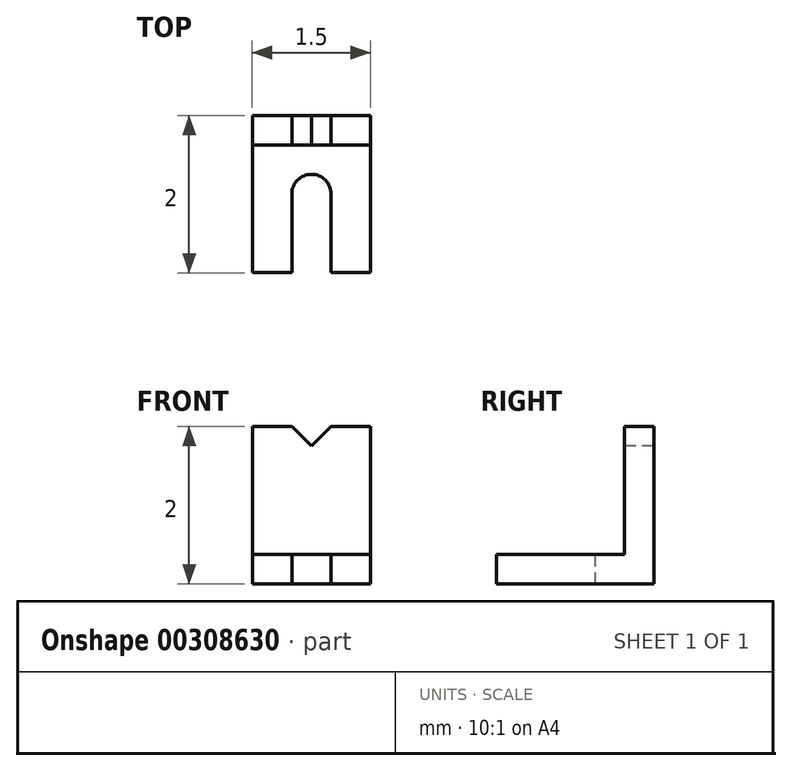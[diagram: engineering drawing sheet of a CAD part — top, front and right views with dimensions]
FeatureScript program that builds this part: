
annotation { "Feature Type Name" : "Feature", "Feature Type Description" : "" }
export const myFeature = defineFeature(function(context is Context, id is Id, definition is map)
    precondition{}
    {
        {
            var Q0;
            Q0=qCreatedBy(makeId("Top.planeOp"),FACE);
            var sketch = newSketch(context, id + "F0", { "sketchPlane" : qUnion([Q0])});
            skLineSegment(sketch, "E0.bottom", {"start": v(-24.74, -5.45) * mm, "end": v(-23.24, -5.45) * mm});
            skLineSegment(sketch, "E0.top", {"start": v(-24.74, -7.45) * mm, "end": v(-24.24, -7.45) * mm});
            skLineSegment(sketch, "E0.left", {"start": v(-24.74, -5.45) * mm, "end": v(-24.74, -7.45) * mm});
            skLineSegment(sketch, "E0.right", {"start": v(-23.24, -5.45) * mm, "end": v(-23.24, -7.45) * mm});
            skPoint(sketch, "E1", {"position": v(-23.74, -7.45) * mm});
            skPoint(sketch, "E2", {"position": v(-24.24, -7.45) * mm});
            skLineSegment(sketch, "E3", {"start": v(-23.74, -7.45) * mm, "end": v(-23.74, -6.45) * mm});
            skLineSegment(sketch, "E4", {"start": v(-24.24, -7.45) * mm, "end": v(-24.24, -6.45) * mm});
            skPoint(sketch, "E5.start.orphan", {"position": v(-23.99, -7.45) * mm});
            skLineSegment(sketch, "E6.trimOffspring", {"start": v(-23.74, -7.45) * mm, "end": v(-23.24, -7.45) * mm});
            skArc(sketch, "E7", {"start": v(-23.74, -6.45) * mm, "mid": v(-23.99, -6.2) * mm, "end": v(-24.24, -6.45) * mm});
            skSolve(sketch);
        }
        {
            var Q0;
            Q0 = qSketchRegion(id + "F0", true);
            extrude(context, id + "F1", {"entities" : qUnion([Q0]), "depth" : .375 * mm});
        }
        {
            var Q0;
            Q0=makeQuery(id+"F1.opExtrude","CAP_FACE",FACE,{"disambiguationData":[OSD([sQuery(id+"F0.wireOp",EDGE,"E0.bottom"),sQuery(id+"F0.wireOp",EDGE,"E0.top"),sQuery(id+"F0.wireOp",EDGE,"E0.left"),sQuery(id+"F0.wireOp",EDGE,"E0.right"),sQuery(id+"F0.wireOp",EDGE,"E3"),sQuery(id+"F0.wireOp",EDGE,"E4"),sQuery(id+"F0.wireOp",EDGE,"IjzjskDy-WpeZ-cA95-hpny-uStXZe4uYbSk"),sQuery(id+"F0.wireOp",EDGE,"E6.trimOffspring")])],"isStart":false});
            var sketch = newSketch(context, id + "F2", { "sketchPlane" : qUnion([Q0])});
            skLineSegment(sketch, "E8.bottom", {"start": v(-24.74, -5.45) * mm, "end": v(-23.24, -5.45) * mm});
            skLineSegment(sketch, "E8.top", {"start": v(-24.74, -5.82) * mm, "end": v(-23.24, -5.82) * mm});
            skLineSegment(sketch, "E8.left", {"start": v(-24.74, -5.45) * mm, "end": v(-24.74, -5.82) * mm});
            skLineSegment(sketch, "E8.right", {"start": v(-23.24, -5.45) * mm, "end": v(-23.24, -5.82) * mm});
            skSolve(sketch);
        }
        {
            var Q0;
            Q0 = qSketchRegion(id + "F2", true);
            extrude(context, id + "F3", {"entities" : qUnion([Q0]), "operationType" : NewBodyOperationType.ADD, "depth" : 1.62 * mm});
        }
        {
            var Q0;
            Q0=makeQuery(id+"F3.opExtrude","SWEPT_FACE",FACE,{"disambiguationData":[OSD([sQuery(id+"F2.wireOp",EDGE,"E8.top")])]});
            var sketch = newSketch(context, id + "F4", { "sketchPlane" : qUnion([Q0])});
            skPoint(sketch, "E9", {"position": v(-24.24, 2) * mm});
            skPoint(sketch, "E10", {"position": v(-23.74, 2) * mm});
            skPoint(sketch, "E11", {"position": v(-23.99, 1.75) * mm});
            skLineSegment(sketch, "E12", {"start": v(-24.24, 2) * mm, "end": v(-23.99, 1.75) * mm});
            skLineSegment(sketch, "E13", {"start": v(-23.74, 2) * mm, "end": v(-23.99, 1.75) * mm});
            skSolve(sketch);
        }
        {
            var Q0;
            {var subQ0=sQuery(id+"F4.wireOp",EDGE,"E12");Q0=makeQuery(id+"F4.imprint","IMPRINT",FACE,{"disambiguationData":[TD([[makeQuery(id+"F4.imprint","IMPRINT",EDGE,{"derivedFrom":subQ0}),1.0]])]});}
            extrude(context, id + "F5", {"entities" : qUnion([Q0]), "operationType" : NewBodyOperationType.REMOVE, "endBound" : BoundingType.UP_TO_NEXT, "oppositeDirection" : true, "depth" : 25 * mm});
        }
    });
